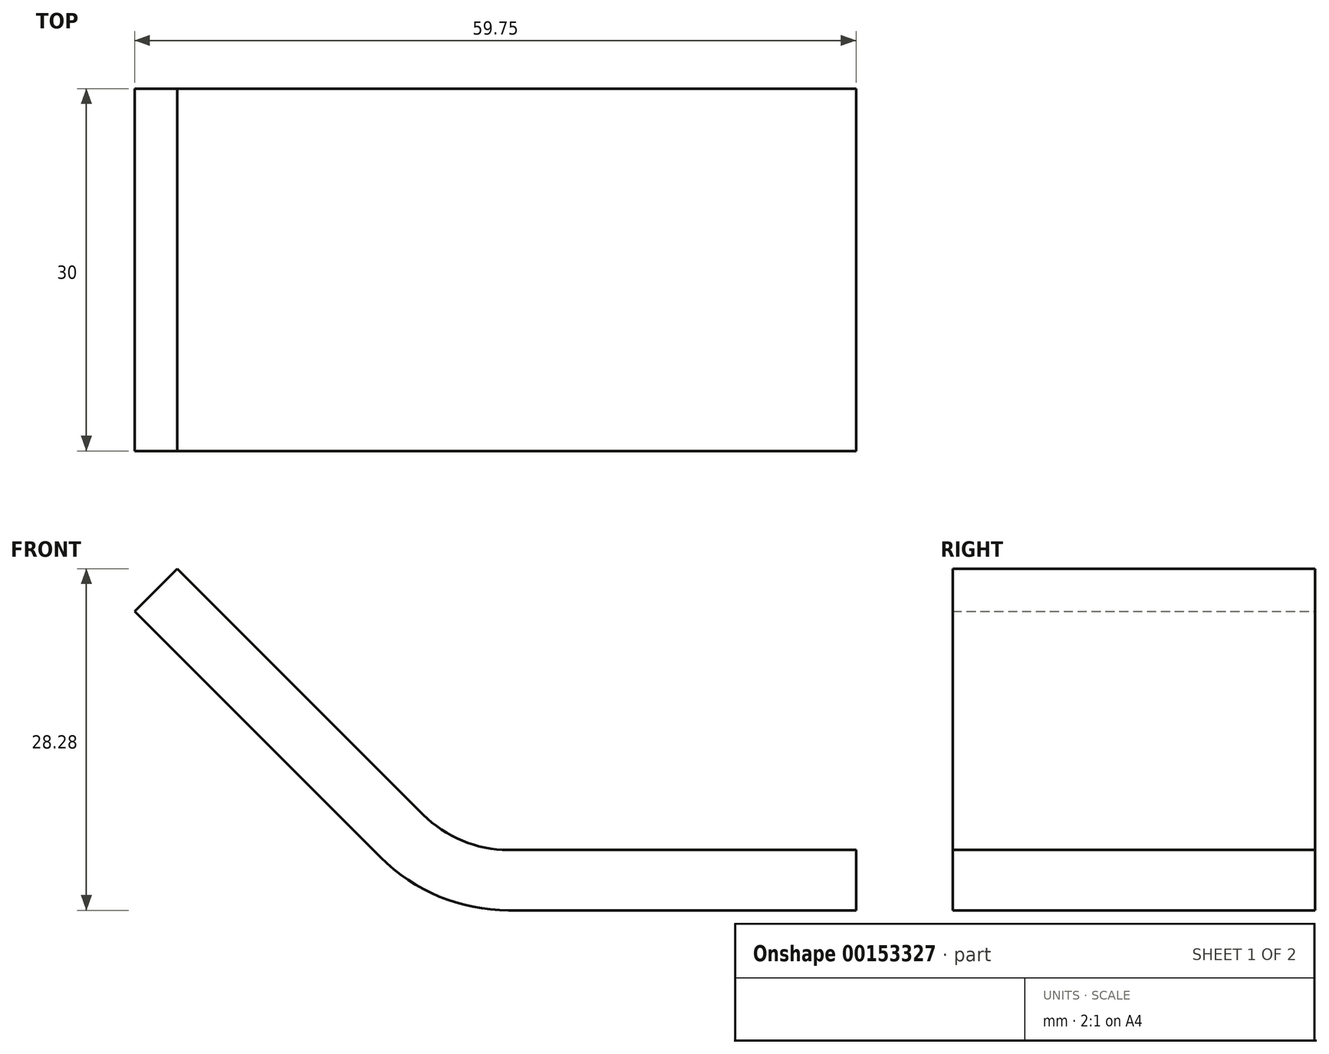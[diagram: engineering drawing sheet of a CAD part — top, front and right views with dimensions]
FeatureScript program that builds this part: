
annotation { "Feature Type Name" : "Feature", "Feature Type Description" : "" }
export const myFeature = defineFeature(function(context is Context, id is Id, definition is map)
    precondition{}
    {
        {
            var Q0;
            Q0=qCreatedBy(makeId("Front.planeOp"),FACE);
            var sketch = newSketch(context, id + "F0", { "sketchPlane" : qUnion([Q0])});
            skLineSegment(sketch, "E0", {"start": v(6.21, 0) * mm, "end": v(35, 0) * mm});
            skLineSegment(sketch, "E1", {"start": v(-4.4, 4.4) * mm, "end": v(-24.75, 24.75) * mm});
            skPoint(sketch, "E2.visualSharp", {"position": v(0, 0) * mm});
            skArc(sketch, "E2.filletArc", {"start": v(-4.4, 4.4) * mm, "mid": v(0.47, 1.14) * mm, "end": v(6.21, 0) * mm});
            skLineSegment(sketch, "E3.0", {"start": v(-0.86, 7.93) * mm, "end": v(-21.21, 28.28) * mm});
            skArc(sketch, "E3.1", {"start": v(-0.86, 7.93) * mm, "mid": v(2.39, 5.76) * mm, "end": v(6.21, 5) * mm});
            skLineSegment(sketch, "E3.2", {"start": v(6.21, 5) * mm, "end": v(35, 5) * mm});
            skLineSegment(sketch, "E4", {"start": v(35, 5) * mm, "end": v(35, 0) * mm});
            skLineSegment(sketch, "E5", {"start": v(-24.75, 24.75) * mm, "end": v(-21.21, 28.28) * mm});
            skPoint(sketch, "E6.orphan", {"position": v(-24.75, 31.82) * mm});
            skSolve(sketch);
        }
        {
            var Q0;
            Q0 = qSketchRegion(id + "F0", true);
            extrude(context, id + "F1", {"entities" : qUnion([Q0]), "depth" : 30 * mm});
        }
    });
